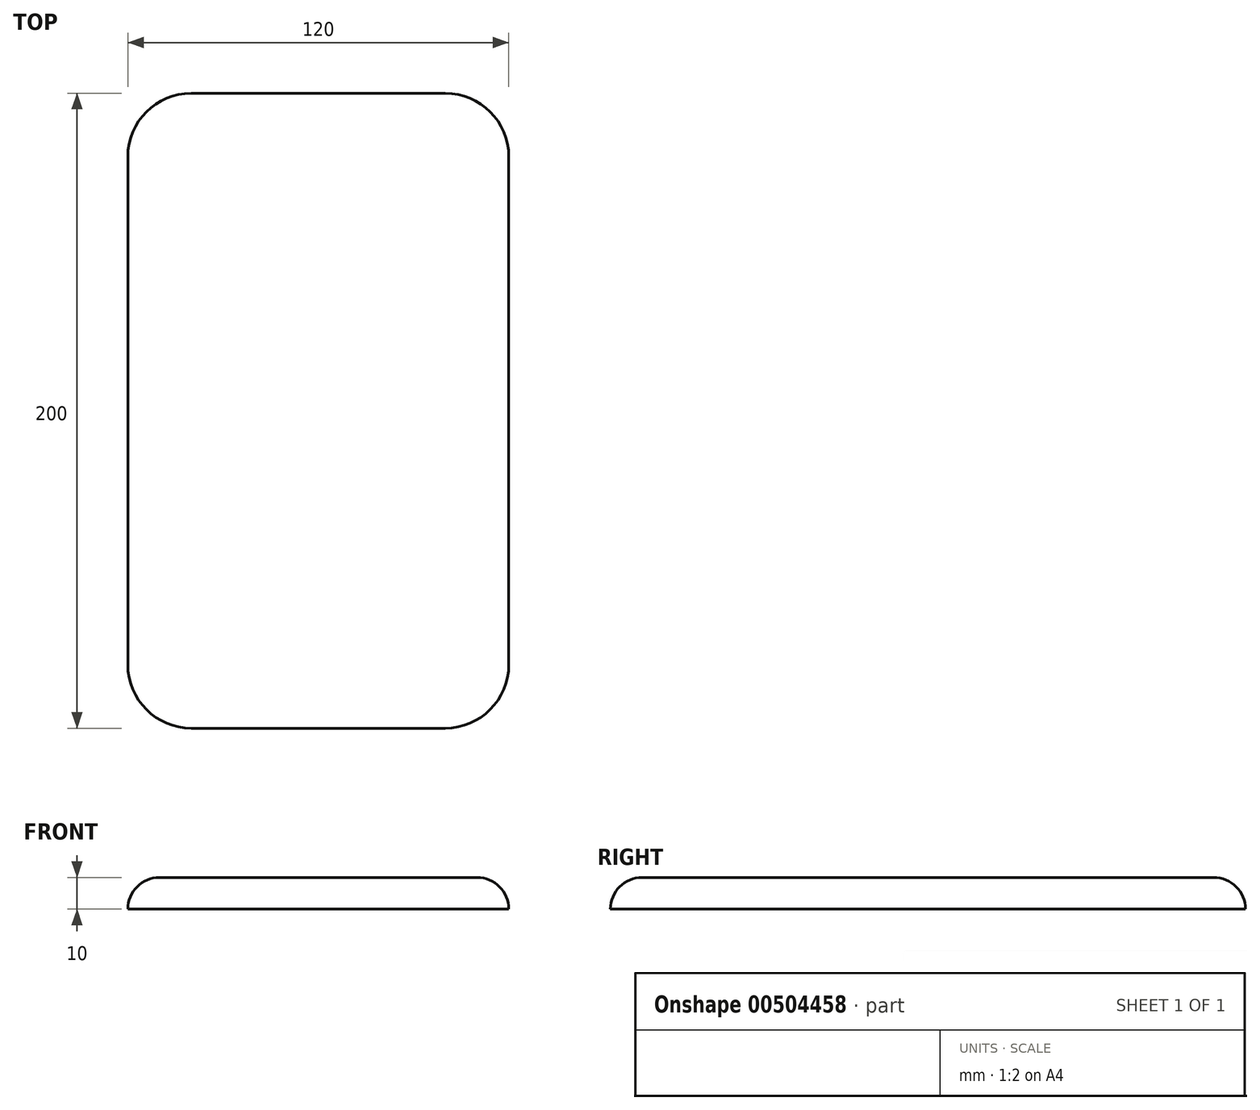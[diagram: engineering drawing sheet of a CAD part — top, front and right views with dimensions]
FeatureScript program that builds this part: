
annotation { "Feature Type Name" : "Feature", "Feature Type Description" : "" }
export const myFeature = defineFeature(function(context is Context, id is Id, definition is map)
    precondition{}
    {
        {
            var Q0;
            Q0=qCreatedBy(makeId("Top.planeOp"),FACE);
            var sketch = newSketch(context, id + "F0", { "sketchPlane" : qUnion([Q0])});
            skLineSegment(sketch, "E0.bottom", {"start": v(-40, 100) * mm, "end": v(40, 100) * mm});
            skLineSegment(sketch, "E0.top", {"start": v(-40, -100) * mm, "end": v(40, -100) * mm});
            skLineSegment(sketch, "E0.left", {"start": v(-60, 80) * mm, "end": v(-60, -80) * mm});
            skLineSegment(sketch, "E0.right", {"start": v(60, 80) * mm, "end": v(60, -80) * mm});
            skPoint(sketch, "E0.middle", {"position": v(0, 0) * mm});
            skPoint(sketch, "E1.visualSharp", {"position": v(-60, 100) * mm});
            skArc(sketch, "E1.filletArc", {"start": v(-40, 100) * mm, "mid": v(-54.14, 94.14) * mm, "end": v(-60, 80) * mm});
            skPoint(sketch, "E2.visualSharp", {"position": v(60, 100) * mm});
            skArc(sketch, "E2.filletArc", {"start": v(60, 80) * mm, "mid": v(54.14, 94.14) * mm, "end": v(40, 100) * mm});
            skPoint(sketch, "E3.visualSharp", {"position": v(-60, -100) * mm});
            skArc(sketch, "E3.filletArc", {"start": v(-60, -80) * mm, "mid": v(-54.14, -94.14) * mm, "end": v(-40, -100) * mm});
            skPoint(sketch, "E4.visualSharp", {"position": v(60, -100) * mm});
            skArc(sketch, "E4.filletArc", {"start": v(40, -100) * mm, "mid": v(54.14, -94.14) * mm, "end": v(60, -80) * mm});
            skSolve(sketch);
        }
        {
            var Q0;
            Q0 = qSketchRegion(id + "F0", true);
            extrude(context, id + "F1", {"entities" : qUnion([Q0]), "depth" : 10 * mm});
        }
        {
            var Q0;
            Q0=makeQuery(id+"F1.opExtrude","CAP_EDGE",EDGE,{"disambiguationData":[OSD([sQuery(id+"F0.wireOp",EDGE,"E0.left")])],"isStart":false});
            fillet(context, id + "F2", {"entities" : qUnion([Q0]), "radius" : 10 * mm, "tangentPropagation" : true, "allowEdgeOverflow" : false});
        }
    });
